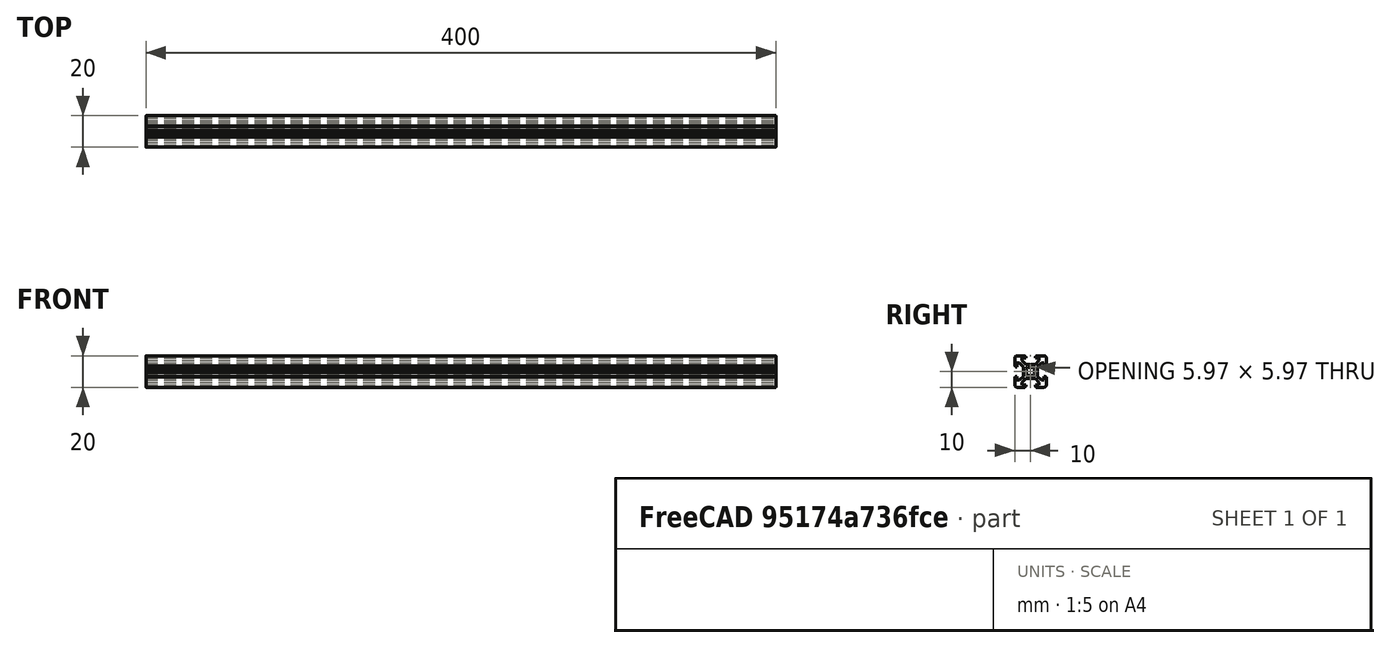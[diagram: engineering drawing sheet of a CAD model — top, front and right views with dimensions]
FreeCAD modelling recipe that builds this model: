
FCSTD DOCUMENT  (FreeCAD 0.19R)
Label: Tslot40
License: All rights reserved
LicenseURL: http://en.wikipedia.org/wiki/All_rights_reserved
objects: Sketcher::SketchObject×1, PartDesign::Pad×1, PartDesign::Body×1
note: 4 computed .brp shape members not serialized (recipe doc carries the construction recipe); baked Part::Feature solids carry a one-line shape summary decoded from their .brp

FEATURE [Sketcher::SketchObject] Sketch  label="T-Slot-Skizze"
  FullyConstrained = true
  MapMode = 5
  Placement = pos=(0,0,0) rot=(0.57735,0.57735,0.57735;2.0944rad)
  Support = -> [YZ_Plane]
  sketch-geometry (98):
    g0: LineSegment StartX=0 StartY=4.1 StartZ=0 EndX=0.65 EndY=4.5 EndZ=0
    g1: LineSegment StartX=0.65 StartY=4.5 StartZ=0 EndX=3 EndY=4.5 EndZ=0
    g2: LineSegment StartX=3 StartY=4.5 StartZ=0 EndX=5.5 EndY=7 EndZ=0
    g3: LineSegment StartX=5.5 StartY=7 StartZ=0 EndX=5.5 EndY=8.5 EndZ=0
    g4: LineSegment StartX=5.5 StartY=8.5 StartZ=0 EndX=3 EndY=8.5 EndZ=0
    g5: LineSegment StartX=3 StartY=8.5 StartZ=0 EndX=3 EndY=9.5 EndZ=0
    g6: LineSegment StartX=3 StartY=9.5 StartZ=0 EndX=3.5 EndY=9.5 EndZ=0
    g7: LineSegment StartX=3.5 StartY=9.5 StartZ=0 EndX=3.5 EndY=10 EndZ=0
    g8: LineSegment StartX=3.5 StartY=10 StartZ=0 EndX=8.5 EndY=10 EndZ=0
    g9: LineSegment StartX=10 StartY=8.5 StartZ=0 EndX=10 EndY=3.5 EndZ=0
    g10: LineSegment StartX=10 StartY=3.5 StartZ=0 EndX=9.5 EndY=3.5 EndZ=0
    g11: LineSegment StartX=9.5 StartY=3.5 StartZ=0 EndX=9.5 EndY=3 EndZ=0
    g12: LineSegment StartX=9.5 StartY=3 StartZ=0 EndX=8.5 EndY=3 EndZ=0
    g13: LineSegment StartX=8.5 StartY=3 StartZ=0 EndX=8.5 EndY=5.5 EndZ=0
    g14: LineSegment StartX=8.5 StartY=5.5 StartZ=0 EndX=7 EndY=5.5 EndZ=0
    g15: LineSegment StartX=7 StartY=5.5 StartZ=0 EndX=4.5 EndY=3 EndZ=0
    g16: LineSegment StartX=4.5 StartY=3 StartZ=0 EndX=4.5 EndY=0.65 EndZ=0
    g17: LineSegment StartX=4.5 StartY=0.65 StartZ=0 EndX=4.1 EndY=0 EndZ=0
    g18: ArcOfCircle CenterX=8.5 CenterY=8.5 CenterZ=0 NormalX=0 NormalY=0 NormalZ=1 AngleXU=0 Radius=1.5 StartAngle=0 EndAngle=1.5708
    g19: LineSegment StartX=0 StartY=-4.1 StartZ=0 EndX=0.65 EndY=-4.5 EndZ=0
    g20: LineSegment StartX=0.65 StartY=-4.5 StartZ=0 EndX=3 EndY=-4.5 EndZ=0
    g21: LineSegment StartX=3 StartY=-4.5 StartZ=0 EndX=5.5 EndY=-7 EndZ=0
    g22: LineSegment StartX=5.5 StartY=-7 StartZ=0 EndX=5.5 EndY=-8.5 EndZ=0
    g23: LineSegment StartX=5.5 StartY=-8.5 StartZ=0 EndX=3 EndY=-8.5 EndZ=0
    g24: LineSegment StartX=3 StartY=-8.5 StartZ=0 EndX=3 EndY=-9.5 EndZ=0
    g25: LineSegment StartX=3 StartY=-9.5 StartZ=0 EndX=3.5 EndY=-9.5 EndZ=0
    g26: LineSegment StartX=3.5 StartY=-9.5 StartZ=0 EndX=3.5 EndY=-10 EndZ=0
    g27: LineSegment StartX=3.5 StartY=-10 StartZ=0 EndX=8.5 EndY=-10 EndZ=0
    g28: LineSegment StartX=10 StartY=-8.5 StartZ=0 EndX=10 EndY=-3.5 EndZ=0
    g29: LineSegment StartX=10 StartY=-3.5 StartZ=0 EndX=9.5 EndY=-3.5 EndZ=0
    g30: LineSegment StartX=9.5 StartY=-3.5 StartZ=0 EndX=9.5 EndY=-3 EndZ=0
    g31: LineSegment StartX=9.5 StartY=-3 StartZ=0 EndX=8.5 EndY=-3 EndZ=0
    g32: LineSegment StartX=8.5 StartY=-3 StartZ=0 EndX=8.5 EndY=-5.5 EndZ=0
    g33: LineSegment StartX=8.5 StartY=-5.5 StartZ=0 EndX=7 EndY=-5.5 EndZ=0
    g34: LineSegment StartX=7 StartY=-5.5 StartZ=0 EndX=4.5 EndY=-3 EndZ=0
    g35: LineSegment StartX=4.5 StartY=-3 StartZ=0 EndX=4.5 EndY=-0.65 EndZ=0
    g36: ArcOfCircle CenterX=8.5 CenterY=-8.5 CenterZ=0 NormalX=0 NormalY=0 NormalZ=1 AngleXU=0 Radius=1.5 StartAngle=4.71239 EndAngle=6.28319
    g37: LineSegment StartX=4.5 StartY=-0.65 StartZ=0 EndX=4.1 EndY=0 EndZ=0
    g38: LineSegment StartX=0 StartY=-4.1 StartZ=0 EndX=-0.65 EndY=-4.5 EndZ=0
    g39: LineSegment StartX=-0.65 StartY=-4.5 StartZ=0 EndX=-3 EndY=-4.5 EndZ=0
    g40: LineSegment StartX=-3 StartY=-4.5 StartZ=0 EndX=-5.5 EndY=-7 EndZ=0
    g41: LineSegment StartX=-5.5 StartY=-7 StartZ=0 EndX=-5.5 EndY=-8.5 EndZ=0
    g42: LineSegment StartX=-5.5 StartY=-8.5 StartZ=0 EndX=-3 EndY=-8.5 EndZ=0
    g43: LineSegment StartX=-3 StartY=-8.5 StartZ=0 EndX=-3 EndY=-9.5 EndZ=0
    g44: LineSegment StartX=-3 StartY=-9.5 StartZ=0 EndX=-3.5 EndY=-9.5 EndZ=0
    g45: LineSegment StartX=-3.5 StartY=-9.5 StartZ=0 EndX=-3.5 EndY=-10 EndZ=0
    g46: LineSegment StartX=-3.5 StartY=-10 StartZ=0 EndX=-8.5 EndY=-10 EndZ=0
    g47: LineSegment StartX=-10 StartY=-8.5 StartZ=0 EndX=-10 EndY=-3.5 EndZ=0
    g48: LineSegment StartX=-10 StartY=-3.5 StartZ=0 EndX=-9.5 EndY=-3.5 EndZ=0
    g49: LineSegment StartX=-9.5 StartY=-3.5 StartZ=0 EndX=-9.5 EndY=-3 EndZ=0
    g50: LineSegment StartX=-9.5 StartY=-3 StartZ=0 EndX=-8.5 EndY=-3 EndZ=0
    g51: LineSegment StartX=-8.5 StartY=-3 StartZ=0 EndX=-8.5 EndY=-5.5 EndZ=0
    g52: LineSegment StartX=-8.5 StartY=-5.5 StartZ=0 EndX=-7 EndY=-5.5 EndZ=0
    g53: LineSegment StartX=-7 StartY=-5.5 StartZ=0 EndX=-4.5 EndY=-3 EndZ=0
    g54: LineSegment StartX=-4.5 StartY=-3 StartZ=0 EndX=-4.5 EndY=-0.65 EndZ=0
    g55: ArcOfCircle CenterX=-8.5 CenterY=-8.5 CenterZ=0 NormalX=0 NormalY=0 NormalZ=1 AngleXU=0 Radius=1.5 StartAngle=3.14159 EndAngle=4.71239
    g56: LineSegment StartX=-4.5 StartY=-0.65 StartZ=0 EndX=-4.1 EndY=0 EndZ=0
    g57: LineSegment StartX=-0.65 StartY=4.5 StartZ=0 EndX=-3 EndY=4.5 EndZ=0
    g58: LineSegment StartX=-3 StartY=4.5 StartZ=0 EndX=-5.5 EndY=7 EndZ=0
    g59: LineSegment StartX=-5.5 StartY=7 StartZ=0 EndX=-5.5 EndY=8.5 EndZ=0
    g60: LineSegment StartX=-5.5 StartY=8.5 StartZ=0 EndX=-3 EndY=8.5 EndZ=0
    g61: LineSegment StartX=-3 StartY=8.5 StartZ=0 EndX=-3 EndY=9.5 EndZ=0
    g62: LineSegment StartX=-3 StartY=9.5 StartZ=0 EndX=-3.5 EndY=9.5 EndZ=0
    g63: LineSegment StartX=-3.5 StartY=9.5 StartZ=0 EndX=-3.5 EndY=10 EndZ=0
    g64: LineSegment StartX=-3.5 StartY=10 StartZ=0 EndX=-8.5 EndY=10 EndZ=0
    g65: LineSegment StartX=-10 StartY=8.5 StartZ=0 EndX=-10 EndY=3.5 EndZ=0
    g66: LineSegment StartX=-10 StartY=3.5 StartZ=0 EndX=-9.5 EndY=3.5 EndZ=0
    g67: LineSegment StartX=-9.5 StartY=3.5 StartZ=0 EndX=-9.5 EndY=3 EndZ=0
    g68: LineSegment StartX=-9.5 StartY=3 StartZ=0 EndX=-8.5 EndY=3 EndZ=0
    g69: LineSegment StartX=-8.5 StartY=3 StartZ=0 EndX=-8.5 EndY=5.5 EndZ=0
    g70: LineSegment StartX=-8.5 StartY=5.5 StartZ=0 EndX=-7 EndY=5.5 EndZ=0
    g71: LineSegment StartX=-7 StartY=5.5 StartZ=0 EndX=-4.5 EndY=3 EndZ=0
    g72: LineSegment StartX=-4.5 StartY=3 StartZ=0 EndX=-4.5 EndY=0.65 EndZ=0
    g73: ArcOfCircle CenterX=-8.5 CenterY=8.5 CenterZ=0 NormalX=0 NormalY=0 NormalZ=1 AngleXU=0 Radius=1.5 StartAngle=1.5708 EndAngle=3.14159
    g74: LineSegment StartX=-4.5 StartY=0.65 StartZ=0 EndX=-4.1 EndY=0 EndZ=0
    g75: LineSegment StartX=0 StartY=4.1 StartZ=0 EndX=-0.65 EndY=4.5 EndZ=0
    g76: Circle CenterX=0 CenterY=0 CenterZ=0 NormalX=0 NormalY=0 NormalZ=1 AngleXU=0 Radius=3.55
    g77: Circle CenterX=0 CenterY=0 CenterZ=0 NormalX=0 NormalY=0 NormalZ=1 AngleXU=0 Radius=2.75
    g78: LineSegment StartX=1.3405 StartY=2.40116 StartZ=0 EndX=1.92324 EndY=2.9839 EndZ=0
    g79: LineSegment StartX=1.92324 StartY=2.9839 StartZ=0 EndX=2.9839 EndY=1.92324 EndZ=0
    g80: LineSegment StartX=2.9839 StartY=1.92324 StartZ=0 EndX=2.40116 EndY=1.3405 EndZ=0
    g81: ArcOfCircle CenterX=0 CenterY=0 CenterZ=0 NormalX=0 NormalY=0 NormalZ=1 AngleXU=0 Radius=2.75 StartAngle=0 EndAngle=0.509172
    g82: ArcOfCircle CenterX=0 CenterY=0 CenterZ=0 NormalX=0 NormalY=0 NormalZ=1 AngleXU=0 Radius=2.75 StartAngle=1.06162 EndAngle=1.5708
    g83: LineSegment StartX=-1.3405 StartY=2.40116 StartZ=0 EndX=-1.92324 EndY=2.9839 EndZ=0
    g84: LineSegment StartX=-1.92324 StartY=2.9839 StartZ=0 EndX=-2.9839 EndY=1.92324 EndZ=0
    g85: LineSegment StartX=-2.9839 StartY=1.92324 StartZ=0 EndX=-2.40116 EndY=1.3405 EndZ=0
    g86: ArcOfCircle CenterX=-1.3e-15 CenterY=6e-16 CenterZ=0 NormalX=0 NormalY=0 NormalZ=1 AngleXU=0 Radius=2.75 StartAngle=2.63242 EndAngle=3.14159
    g87: ArcOfCircle CenterX=-1.3e-15 CenterY=6e-16 CenterZ=0 NormalX=0 NormalY=0 NormalZ=1 AngleXU=0 Radius=2.75 StartAngle=1.5708 EndAngle=2.07997
    g88: LineSegment StartX=-1.34051 StartY=-2.40115 StartZ=0 EndX=-1.92325 EndY=-2.98389 EndZ=0
    g89: LineSegment StartX=-1.92325 StartY=-2.98389 StartZ=0 EndX=-2.9839 EndY=-1.92323 EndZ=0
    g90: LineSegment StartX=-2.9839 StartY=-1.92323 StartZ=0 EndX=-2.40116 EndY=-1.34049 EndZ=0
    g91: ArcOfCircle CenterX=-3e-16 CenterY=2e-16 CenterZ=0 NormalX=0 NormalY=0 NormalZ=1 AngleXU=0 Radius=2.75 StartAngle=3.14159 EndAngle=3.65076
    g92: ArcOfCircle CenterX=-3e-16 CenterY=2e-16 CenterZ=0 NormalX=0 NormalY=0 NormalZ=1 AngleXU=0 Radius=2.75 StartAngle=4.20321 EndAngle=4.71239
    g93: LineSegment StartX=1.34051 StartY=-2.40115 StartZ=0 EndX=1.92325 EndY=-2.98389 EndZ=0
    g94: LineSegment StartX=1.92325 StartY=-2.98389 StartZ=0 EndX=2.9839 EndY=-1.92323 EndZ=0
    g95: LineSegment StartX=2.9839 StartY=-1.92323 StartZ=0 EndX=2.40116 EndY=-1.34049 EndZ=0
    g96: ArcOfCircle CenterX=3e-16 CenterY=2e-16 CenterZ=0 NormalX=0 NormalY=0 NormalZ=1 AngleXU=0 Radius=2.75 StartAngle=4.71239 EndAngle=5.22156
    g97: ArcOfCircle CenterX=3e-16 CenterY=2e-16 CenterZ=0 NormalX=0 NormalY=0 NormalZ=1 AngleXU=0 Radius=2.75 StartAngle=5.77402 EndAngle=6.28319
  constraints (291):
    c: PointOnObject(g0,g-2)
    c: Coincident(g0,g1)
    c: Horizontal(g1)
    c: Coincident(g1,g2)
    c: Coincident(g2,g3)
    c: Vertical(g3)
    c: Coincident(g3,g4)
    c: Horizontal(g4)
    c: Coincident(g4,g5)
    c: Vertical(g5)
    c: Coincident(g5,g6)
    c: Horizontal(g6)
    c: Coincident(g6,g7)
    c: Coincident(g7,g8)
    c: Horizontal(g8)
    c: Vertical(g7)
    c: DistanceX(g-1,g5) = 3
    c: DistanceY(g4,g7) = 1.5
    c: DistanceY(g0,g7) = 5.5
    c: DistanceY(g3,g3) = 1.5
    c: DistanceY(g4,g5) = 1
    c: DistanceX(g-1,g1) = 3
    c: DistanceX(g-1,g7) = 3.5
    c: DistanceX(g0,g0) = 0.65
    c: DistanceY(g0,g0) = 0.4
    c: DistanceX(g-1,g3) = 5.5
    c: Vertical(g9)
    c: Coincident(g9,g10)
    c: Coincident(g10,g11)
    c: Coincident(g11,g12)
    c: Coincident(g12,g13)
    c: Vertical(g13)
    c: Coincident(g13,g14)
    c: Horizontal(g14)
    c: Coincident(g14,g15)
    c: Coincident(g15,g16)
    c: Vertical(g16)
    c: Coincident(g16,g17)
    c: PointOnObject(g17,g-1)
    c: Horizontal(g10)
    c: Horizontal(g12)
    c: Vertical(g11)
    c: Equal(g17,g0)
    c: Equal(g1,g16)
    c: Equal(g15,g2)
    c: Equal(g3,g14)
    c: Equal(g13,g4)
    c: Equal(g12,g5)
    c: Parallel(g15,g2)
    c: Equal(g11,g6)
    c: Equal(g10,g7)
    c: Equal(g9,g8)
    c: Tangent(g8,g18) = 1.5708
    c: Tangent(g9,g18) = 1.5708
    c: Radius(g18) = 1.5
    c: DistanceY(g-1,g8) = 10
    c: DistanceX(g-1,g9) = 10
    c: Coincident(g19,g20)
    c: Horizontal(g20)
    c: Coincident(g20,g21)
    c: Coincident(g21,g22)
    c: Vertical(g22)
    c: Coincident(g22,g23)
    c: Horizontal(g23)
    c: Coincident(g23,g24)
    c: Vertical(g24)
    c: Coincident(g24,g25)
    c: Horizontal(g25)
    c: Coincident(g25,g26)
    c: Coincident(g26,g27)
    c: Horizontal(g27)
    c: Vertical(g26)
    c: Vertical(g28)
    c: Coincident(g28,g29)
    c: Coincident(g29,g30)
    c: Coincident(g30,g31)
    c: Coincident(g31,g32)
    c: Vertical(g32)
    c: Coincident(g32,g33)
    c: Horizontal(g33)
    c: Coincident(g33,g34)
    c: Coincident(g34,g35)
    c: Vertical(g35)
    c: Coincident(g35,g37)
    c: Horizontal(g29)
    c: Horizontal(g31)
    c: Vertical(g30)
    c: Equal(g37,g19)
    c: Equal(g20,g35)
    c: Equal(g34,g21)
    c: Equal(g22,g33)
    c: Equal(g32,g23)
    c: Equal(g31,g24)
    c: Parallel(g34,g21)
    c: Equal(g30,g25)
    c: Equal(g29,g26)
    c: Equal(g28,g27)
    c: Tangent(g27,g36) = -1.5708
    c: Tangent(g28,g36) = -1.5708
    c: Radius(g36) = 1.5
    c: Equal(g9,g28)
    c: Equal(g12,g31)
    c: DistanceX(g-1,g28) = 10
    c: DistanceY(g27,g-1) = 10
    c: DistanceY(g30,g-1) = 3
    c: Equal(g33,g14)
    c: Equal(g35,g16)
    c: Equal(g17,g37)
    c: Coincident(g37,g17)
    c: Equal(g15,g34)
    c: PointOnObject(g19,g-2)
    c: DistanceY(g34,g-1) = 3
    c: DistanceX(g-1,g20) = 3
    c: Coincident(g38,g39)
    c: Horizontal(g39)
    c: Coincident(g39,g40)
    c: Coincident(g40,g41)
    c: Vertical(g41)
    c: Coincident(g41,g42)
    c: Horizontal(g42)
    c: Coincident(g42,g43)
    c: Vertical(g43)
    c: Coincident(g43,g44)
    c: Horizontal(g44)
    c: Coincident(g44,g45)
    c: Coincident(g45,g46)
    c: Horizontal(g46)
    c: Vertical(g45)
    c: Vertical(g47)
    c: Coincident(g47,g48)
    c: Coincident(g48,g49)
    c: Coincident(g49,g50)
    c: Coincident(g50,g51)
    c: Vertical(g51)
    c: Coincident(g51,g52)
    c: Horizontal(g52)
    c: Coincident(g52,g53)
    c: Coincident(g53,g54)
    c: Vertical(g54)
    c: Coincident(g54,g56)
    c: Horizontal(g48)
    c: Horizontal(g50)
    c: Vertical(g49)
    c: Equal(g39,g54)
    c: Equal(g53,g40)
    c: Equal(g41,g52)
    c: Equal(g51,g42)
    c: Equal(g50,g43)
    c: Parallel(g53,g40)
    c: Equal(g49,g44)
    c: Equal(g48,g45)
    c: Equal(g47,g46)
    c: Tangent(g46,g55) = 1.5708
    c: Tangent(g47,g55) = 1.5708
    c: Radius(g55) = 1.5
    c: Coincident(g38,g19)
    c: DistanceX(g39,g-1) = 3
    c: DistanceX(g38,g19) = 0.65
    c: DistanceY(g38,g19) = 0.4
    c: PointOnObject(g56,g-1)
    c: Equal(g56,g38)
    c: DistanceY(g53,g-1) = 3
    c: Equal(g22,g41)
    c: Equal(g42,g23)
    c: Equal(g24,g43)
    c: Equal(g25,g44)
    c: Equal(g26,g45)
    c: DistanceY(g46,g-1) = 10
    c: DistanceX(g47,g-1) = 10
    c: Coincident(g75,g57)
    c: Horizontal(g57)
    c: Coincident(g57,g58)
    c: Coincident(g58,g59)
    c: Vertical(g59)
    c: Coincident(g59,g60)
    c: Horizontal(g60)
    c: Coincident(g60,g61)
    c: Vertical(g61)
    c: Coincident(g61,g62)
    c: Horizontal(g62)
    c: Coincident(g62,g63)
    c: Coincident(g63,g64)
    c: Horizontal(g64)
    c: Vertical(g63)
    c: Vertical(g65)
    c: Coincident(g65,g66)
    c: Coincident(g66,g67)
    c: Coincident(g67,g68)
    c: Coincident(g68,g69)
    c: Vertical(g69)
    c: Coincident(g69,g70)
    c: Horizontal(g70)
    c: Coincident(g70,g71)
    c: Coincident(g71,g72)
    c: Vertical(g72)
    c: Coincident(g72,g74)
    c: Horizontal(g66)
    c: Horizontal(g68)
    c: Vertical(g67)
    c: Equal(g57,g72)
    c: Equal(g71,g58)
    c: Equal(g59,g70)
    c: Equal(g69,g60)
    c: Equal(g68,g61)
    c: Parallel(g71,g58)
    c: Equal(g67,g62)
    c: Equal(g66,g63)
    c: Equal(g65,g64)
    c: Tangent(g64,g73) = -1.5708
    c: Tangent(g65,g73) = -1.5708
    c: Radius(g73) = 1.5
    c: Equal(g74,g75)
    c: Coincident(g56,g74)
    c: Coincident(g0,g75)
    c: Equal(g0,g75)
    c: Equal(g1,g57)
    c: Equal(g2,g58)
    c: Equal(g3,g59)
    c: Equal(g4,g60)
    c: Equal(g5,g61)
    c: Equal(g6,g62)
    c: Equal(g7,g63)
    c: Equal(g8,g64)
    c: DistanceX(g65,g-1) = 10
    c: Coincident(g76,g-1)
    c: Coincident(g77,g-1)
    c: Radius(g76) = 3.55
    c: Radius(g77) = 2.75
    c: PointOnObject(g78,g77)
    c: PointOnObject(g78,g76)
    c: Coincident(g78,g79)
    c: PointOnObject(g79,g76)
    c: Coincident(g79,g80)
    c: PointOnObject(g80,g77)
    c: Coincident(g81,g-1)
    c: Coincident(g81,g80)
    c: Coincident(g82,g81)
    c: Coincident(g82,g78)
    c: Parallel(g78,g80)
    c: Parallel(g78,g2)
    c: Distance(g79) = 1.5
    c: Distance(g78,g80) = 1.5
    c: PointOnObject(g82,g-2)
    c: PointOnObject(g81,g-1)
    c: Coincident(g83,g84)
    c: Coincident(g84,g85)
    c: Coincident(g86,g85)
    c: Coincident(g87,g86)
    c: Coincident(g87,g83)
    c: Parallel(g83,g85)
    c: Distance(g84) = 1.5
    c: Distance(g83,g85) = 1.5
    c: Coincident(g82,g87)
    c: PointOnObject(g86,g-1)
    c: PointOnObject(g83,g76)
    c: PointOnObject(g83,g77)
    c: PointOnObject(g85,g77)
    c: PointOnObject(g84,g76)
    c: PointOnObject(g86,g77)
    c: Parallel(g85,g71)
    c: Coincident(g88,g89)
    c: Coincident(g89,g90)
    c: Coincident(g91,g90)
    c: Coincident(g92,g91)
    c: Coincident(g92,g88)
    c: Parallel(g88,g90)
    c: Distance(g89) = 1.5
    c: Distance(g88,g90) = 1.5
    c: PointOnObject(g88,g77)
    c: PointOnObject(g90,g77)
    c: Coincident(g86,g91)
    c: PointOnObject(g89,g76)
    c: PointOnObject(g88,g76)
    c: PointOnObject(g92,g-2)
    c: PointOnObject(g92,g77)
    c: Parallel(g88,g40)
    c: Coincident(g93,g94)
    c: Coincident(g94,g95)
    c: Coincident(g97,g95)
    c: Coincident(g96,g97)
    c: Coincident(g96,g93)
    c: Parallel(g93,g95)
    c: Distance(g94) = 1.5
    c: Distance(g93,g95) = 1.5
    c: Coincident(g81,g97)
    c: Coincident(g92,g96)
    c: PointOnObject(g93,g77)
    c: PointOnObject(g95,g77)
    c: PointOnObject(g94,g76)
    c: PointOnObject(g93,g76)
    c: Parallel(g93,g21)
FEATURE [PartDesign::Pad] Pad  label="T-Slot-Element"
  Direction = (1,1,1)
  Length = 400
  Length2 = 100
  Placement = pos=(0,0,0) rot=(0.57735,0.57735,0.57735;2.0944rad)
  Profile = -> Sketch
  Type = 0
FEATURE [PartDesign::Body] Body  label="T-Slot-Profil 20x20"
  Group = -> [Sketch,Pad]
  Origin = -> Origin
  Tip = -> Pad
